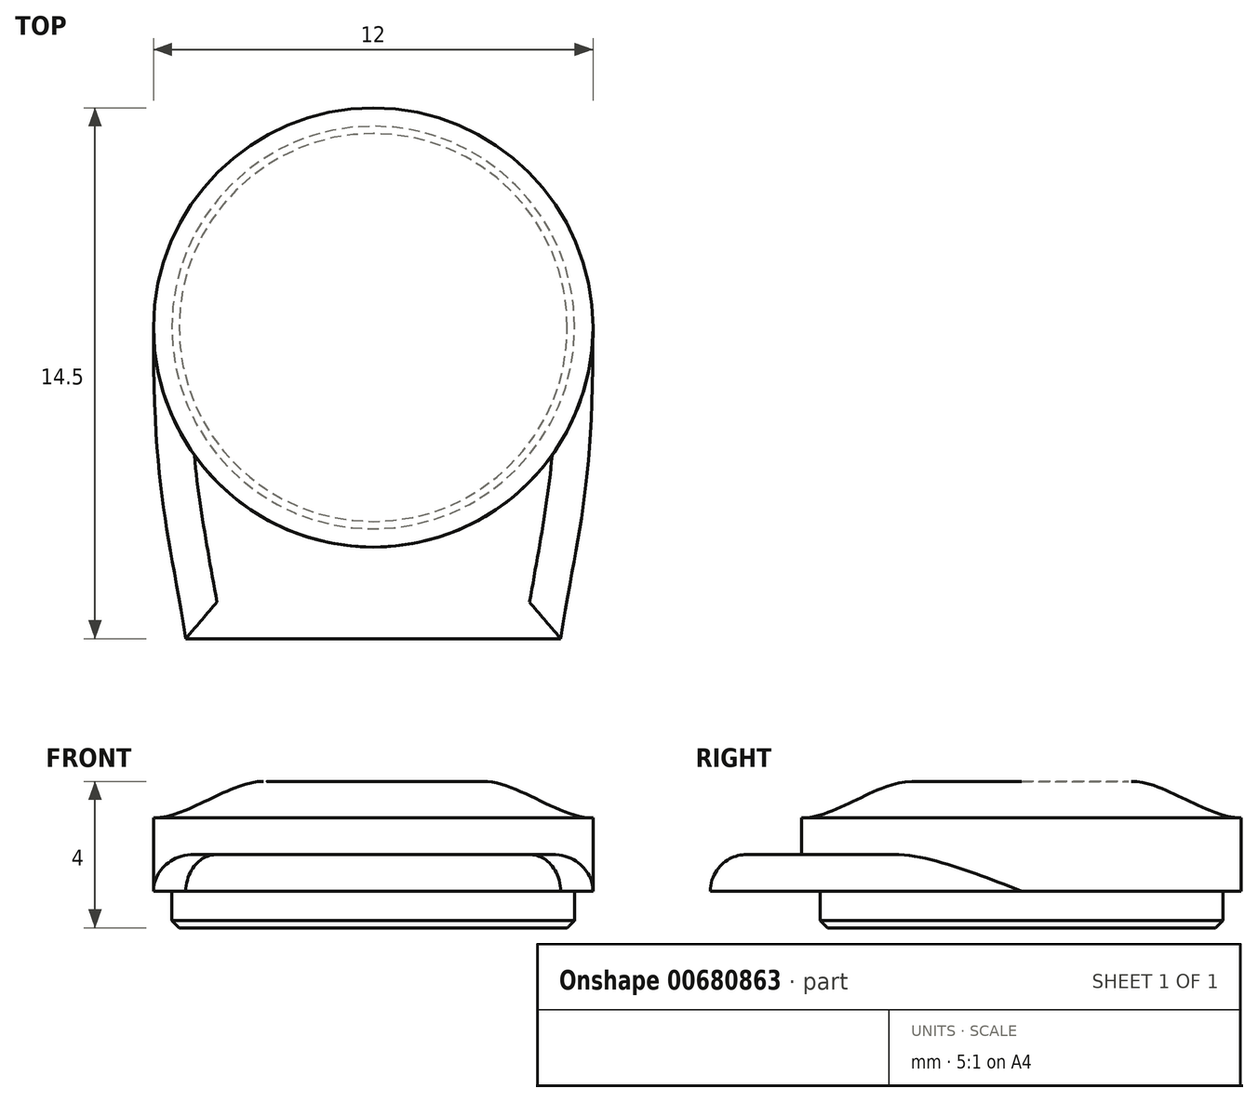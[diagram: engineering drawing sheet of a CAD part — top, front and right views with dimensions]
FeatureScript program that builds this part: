
annotation { "Feature Type Name" : "Feature", "Feature Type Description" : "" }
export const myFeature = defineFeature(function(context is Context, id is Id, definition is map)
    precondition{}
    {
        {
            var Q0;
            Q0=qCreatedBy(makeId("Top.planeOp"),FACE);
            var sketch = newSketch(context, id + "F0", { "sketchPlane" : qUnion([Q0])});
            skCircle(sketch, "E0", {"center": v(0, 0) * mm, "radius": 6 * mm});
            skLineSegment(sketch, "E1.top", {"start": v(-5.12, -8.5) * mm, "end": v(5.12, -8.5) * mm});
            skCircle(sketch, "E2", {"center": v(0, 0) * mm, "radius": 3 * mm});
            skCircle(sketch, "E3", {"center": v(0, 0) * mm, "radius": 5.5 * mm});
            skFitSpline(sketch, "E4", {"points": [v(-6, 0) * mm, v(-5.12, -8.5) * mm], "startDerivative": vector(0, -13.62) * mm, "endDerivative": vector(1.52, -9.52) * mm});
            skFitSpline(sketch, "E5.MirrorCS", {"points": [v(6, 0) * mm, v(5.12, -8.5) * mm], "startDerivative": vector(0, -13.62) * mm, "endDerivative": vector(-1.52, -9.52) * mm});
            skSolve(sketch);
        }
        {
            var Q0;
            Q0=makeQuery(id+"F0.imprint","IMPRINT",FACE,{"disambiguationData":[TD([[makeQuery(id+"F0.imprint","IMPRINT",EDGE,{"derivedFrom":sQuery(id+"F0.wireOp",EDGE,"E2")}),1.0]])]});
            extrude(context, id + "F1", {"entities" : qUnion([Q0]), "depth" : 3 * mm, "offsetDistance" : 25.4 * mm});
        }
        {
            var Q0;
            Q0=makeQuery(id+"F0.imprint","IMPRINT",FACE,{"disambiguationData":[TD([[makeQuery(id+"F0.imprint","IMPRINT",EDGE,{"derivedFrom":sQuery(id+"F0.wireOp",EDGE,"E2")}),-1.0]])]});
            var Q1;
            Q1=makeQuery(id+"F0.imprint","IMPRINT",FACE,{"disambiguationData":[TD([[makeQuery(id+"F0.imprint","IMPRINT",EDGE,{"derivedFrom":sQuery(id+"F0.wireOp",EDGE,"E3")}),-1.0]])]});
            extrude(context, id + "F2", {"entities" : qUnion([Q0, Q1]), "operationType" : NewBodyOperationType.ADD, "depth" : 2 * mm, "offsetDistance" : 25.4 * mm});
        }
        {
            var Q0;
            Q0=qCreatedBy(makeId("Front.planeOp"),FACE);
            var sketch = newSketch(context, id + "F3", { "sketchPlane" : qUnion([Q0])});
            skLineSegment(sketch, "E6", {"start": v(6, 2) * mm, "end": v(3, 2) * mm});
            skLineSegment(sketch, "E7", {"start": v(3, 2) * mm, "end": v(3, 3) * mm});
            skFitSpline(sketch, "E8", {"points": [v(3, 3) * mm, v(6, 2) * mm], "startDerivative": vector(2.77, 0) * mm, "endDerivative": vector(2.8, 0) * mm});
            skSolve(sketch);
        }
        {
            var Q0;
            Q0=makeQuery(id+"F3.imprint","IMPRINT",FACE,{"disambiguationData":[TD([[makeQuery(id+"F3.imprint","IMPRINT",EDGE,{"derivedFrom":sQuery(id+"F3.wireOp",EDGE,"E6")}),-1.0]])]});
            var Q1;
            Q1=makeQuery(id+"F1.opExtrude","SWEPT_FACE",FACE,{"disambiguationData":[OSD([sQuery(id+"F0.wireOp",EDGE,"E2")])]});
            revolve(context, id + "F4", {"operationType" : NewBodyOperationType.ADD, "entities" : qUnion([Q0]), "axis" : qUnion([Q1]), "revolveType" : RevolveType.FULL});
        }
        {
            var Q0;
            Q0=makeQuery(id+"F0.imprint","IMPRINT",FACE,{"disambiguationData":[TD([[makeQuery(id+"F0.imprint","IMPRINT",EDGE,{"derivedFrom":sQuery(id+"F0.wireOp",EDGE,"E2")}),-1.0]])]});
            var Q1;
            Q1=makeQuery(id+"F0.imprint","IMPRINT",FACE,{"disambiguationData":[TD([[makeQuery(id+"F0.imprint","IMPRINT",EDGE,{"derivedFrom":sQuery(id+"F0.wireOp",EDGE,"E2")}),1.0]])]});
            extrude(context, id + "F5", {"entities" : qUnion([Q0, Q1]), "operationType" : NewBodyOperationType.ADD, "depth" : -1 * mm, "offsetDistance" : 25.4 * mm});
        }
        {
            var Q0;
            Q0=makeQuery(id+"F5.opExtrude","CAP_EDGE",EDGE,{"disambiguationData":[OSD([sQuery(id+"F0.wireOp",EDGE,"E3")])],"isStart":false});
            chamfer(context, id + "F6", {"entities" : qUnion([Q0]), "width" : 0.2 * mm, "tangentPropagation" : true});
        }
        {
            var Q0;
            Q0=makeQuery(id+"F0.imprint","IMPRINT",FACE,{"disambiguationData":[TD([[makeQuery(id+"F0.imprint","IMPRINT",EDGE,{"derivedFrom":sQuery(id+"F0.wireOp",EDGE,"E1.top")}),1.0]])]});
            extrude(context, id + "F7", {"entities" : qUnion([Q0]), "operationType" : NewBodyOperationType.ADD, "depth" : 1 * mm, "offsetDistance" : 25 * mm});
        }
        {
            var Q0;
            Q0=makeQuery(id+"F7.opExtrude","CAP_EDGE",EDGE,{"disambiguationData":[OSD([sQuery(id+"F0.wireOp",EDGE,"E4")])],"isStart":false});
            var Q1;
            Q1=makeQuery(id+"F7.opExtrude","CAP_EDGE",EDGE,{"disambiguationData":[OSD([sQuery(id+"F0.wireOp",EDGE,"E1.top")])],"isStart":false});
            var Q2;
            Q2=makeQuery(id+"F7.opExtrude","CAP_EDGE",EDGE,{"disambiguationData":[OSD([sQuery(id+"F0.wireOp",EDGE,"E5.MirrorCS")])],"isStart":false});
            fillet(context, id + "F8", {"entities" : qUnion([Q0, Q1, Q2]), "radius" : 1 * mm, "tangentPropagation" : true, "allowEdgeOverflow" : false});
        }
    });
